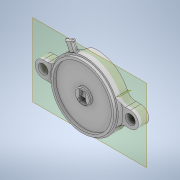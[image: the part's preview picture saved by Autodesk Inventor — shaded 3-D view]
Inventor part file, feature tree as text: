
AUTODESK INVENTOR PART (.ipt)
format: ipt  version: 2021.3 (Build 253353010, 353A)  size: 439,296 bytes
history: native  units: mm
features: extrude x8, sketch x8, fillet x5, plane x2
ambient origin geometry x8: Origin, YZ Plane, XZ Plane, XY Plane, X Axis, Y Axis, Z Axis, Center Point
bodies: Volumenkörper1 (feature_tree)
feature tree (23):
  extrude  "Extrusion1"  Depth=10.0mm TaperAngle=0.0deg
  extrude  "Extrusion2"  Depth=10.3mm
  extrude  "Extrusion3"  Depth=1.25mm
  extrude  "Extrusion4"  Depth=5.5mm
  extrude  "Extrusion5"  Depth=1.1mm
  extrude  "Extrusion6"  Depth=2.0mm TaperAngle=0.0deg
  plane  "Arbeitsebene1"
  extrude  "Extrusion7"  Depth=0.5mm TaperAngle=0.0deg
  plane  "Arbeitsebene2"
  extrude  "Extrusion8"  Depth=0.5mm TaperAngle=0.0deg
  fillet  "Rundung1"  Radius=6.6mm
  fillet  "Rundung2"  Radius=7.0mm
  fillet  "Rundung3"  Radius=5.5mm
  fillet  "Rundung4"  Radius=7.0mm
  fillet  "Rundung5"  Radius=5.0mm
  sketch  "Skizze1"  dims[d0=45.0mm d1=10.0mm d2=0.0mm]
  sketch  "Skizze2"  dims[d3=39.3mm d4=10.3mm]
  sketch  "Skizze3"  dims[d5=1.8mm d6=0.0mm d7=1.25mm]
  sketch  "Skizze4"  dims[d8=4.2mm d9=5.5mm]
  sketch  "Skizze5"  dims[d12=2.2mm d13=1.1mm]
  sketch  "Skizze6"  dims[d14=3.7mm d15=2.0mm d16=0.0mm]
  sketch  "Skizze7"  dims[d17=0.5mm d18=2.0mm d19=0.0mm]
  sketch  "Skizze8"  dims[d20=24.0mm d21=5.0mm d22=0.0mm d23=6.6mm d25=7.0mm d26=5.5mm d27=7.0mm d28=0.0mm d29=5.0mm d31=0.0mm d32=0.0mm d33=5.0mm d34=5.0mm d36=0.5mm d37=0.523831mm d40=3.0mm d41=0.0mm d42=2.0mm d43=2.0mm d45=1.0mm d46=1.2mm d47=2.0mm d48=0.1mm d49=0.5mm]
